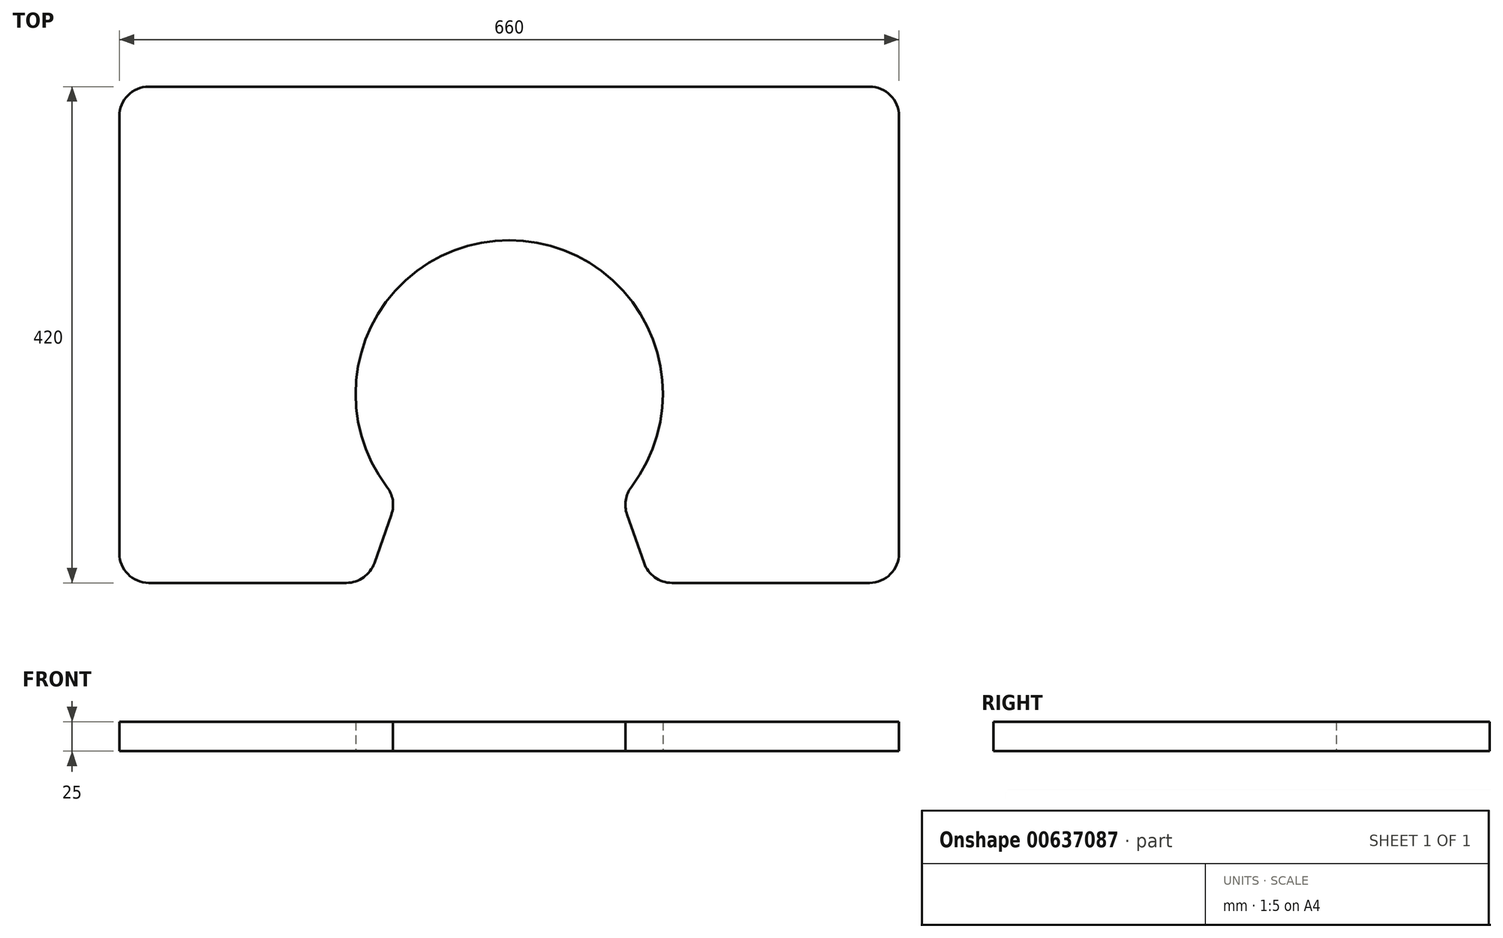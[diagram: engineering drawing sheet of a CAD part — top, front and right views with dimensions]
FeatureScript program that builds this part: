
annotation { "Feature Type Name" : "Feature", "Feature Type Description" : "" }
export const myFeature = defineFeature(function(context is Context, id is Id, definition is map)
    precondition{}
    {
        {
            var Q0;
            Q0=qCreatedBy(makeId("Top.planeOp"),FACE);
            var sketch = newSketch(context, id + "F0", { "sketchPlane" : qUnion([Q0])});
            skLineSegment(sketch, "E0.bottom", {"start": v(330, 210) * mm, "end": v(-330, 210) * mm});
            skLineSegment(sketch, "E0.top", {"start": v(330, -210) * mm, "end": v(-330, -210) * mm});
            skLineSegment(sketch, "E0.left", {"start": v(330, 210) * mm, "end": v(330, -210) * mm});
            skLineSegment(sketch, "E0.right", {"start": v(-330, 210) * mm, "end": v(-330, -210) * mm});
            skPoint(sketch, "E0.middle", {"position": v(0, 0) * mm});
            skCircle(sketch, "E1", {"center": v(0.03, -50) * mm, "radius": 130 * mm});
            skLineSegment(sketch, "E2", {"start": v(-120, -210) * mm, "end": v(-94.96, -138.76) * mm});
            skLineSegment(sketch, "E3", {"start": v(120, -210) * mm, "end": v(95.04, -138.73) * mm});
            skPoint(sketch, "E4", {"position": v(0, -210) * mm});
            skSolve(sketch);
        }
        {
            var Q0;
            Q0=makeQuery(id+"F0.imprint","IMPRINT",FACE,{"disambiguationData":[TD([[makeQuery(id+"F0.imprint","IMPRINT",EDGE,{"derivedFrom":sQuery(id+"F0.wireOp",EDGE,"E0.bottom")}),1.0]])]});
            extrude(context, id + "F1", {"entities" : qUnion([Q0]), "depth" : 25 * mm});
        }
        {
            var Q0;
            Q0=makeQuery(id+"F1.opExtrude","SWEPT_EDGE",EDGE,{"disambiguationData":[OSD([sQuery(id+"F0.wireOp",EDGE,"E1"),sQuery(id+"F0.wireOp",EDGE,"8K2nLb33-7zb7-YIVY-jQB5-7TyeZ0Rkaev6")])]});
            var Q1;
            Q1=makeQuery(id+"F1.opExtrude","SWEPT_EDGE",EDGE,{"disambiguationData":[OSD([sQuery(id+"F0.wireOp",EDGE,"E1"),sQuery(id+"F0.wireOp",EDGE,"b5508e05-085b-4176-a4c3-e73228444c430.MirrorCS")])]});
            var Q2;
            Q2=makeQuery(id+"F1.opExtrude","SWEPT_EDGE",EDGE,{"disambiguationData":[OSD([sQuery(id+"F0.wireOp",EDGE,"E0.top"),sQuery(id+"F0.wireOp",EDGE,"b5508e05-085b-4176-a4c3-e73228444c430.MirrorCS"),sQuery(id+"F0.wireOp",EDGE,"b5508e05-085b-4176-a4c3-e73228444c431.MirrorCS")])]});
            var Q3;
            Q3=makeQuery(id+"F1.opExtrude","SWEPT_EDGE",EDGE,{"disambiguationData":[OSD([sQuery(id+"F0.wireOp",EDGE,"E0.top"),sQuery(id+"F0.wireOp",EDGE,"E0.left")])]});
            var Q4;
            Q4=makeQuery(id+"F1.opExtrude","SWEPT_EDGE",EDGE,{"disambiguationData":[OSD([sQuery(id+"F0.wireOp",EDGE,"E0.top"),sQuery(id+"F0.wireOp",EDGE,"8K2nLb33-7zb7-YIVY-jQB5-7TyeZ0Rkaev6"),sQuery(id+"F0.wireOp",EDGE,"ovbGFed6-ZiOo-55EP-2kew-Z5asyUi1s6AM")])]});
            var Q5;
            Q5=makeQuery(id+"F1.opExtrude","SWEPT_EDGE",EDGE,{"disambiguationData":[OSD([sQuery(id+"F0.wireOp",EDGE,"E0.top"),sQuery(id+"F0.wireOp",EDGE,"E0.right")])]});
            var Q6;
            Q6=makeQuery(id+"F1.opExtrude","SWEPT_EDGE",EDGE,{"disambiguationData":[OSD([sQuery(id+"F0.wireOp",EDGE,"E0.bottom"),sQuery(id+"F0.wireOp",EDGE,"E0.left")])]});
            var Q7;
            Q7=makeQuery(id+"F1.opExtrude","SWEPT_EDGE",EDGE,{"disambiguationData":[OSD([sQuery(id+"F0.wireOp",EDGE,"E0.bottom"),sQuery(id+"F0.wireOp",EDGE,"E0.right")])]});
            fillet(context, id + "F2", {"entities" : qUnion([Q0, Q1, Q2, Q3, Q4, Q5, Q6, Q7]), "radius" : 25 * mm, "tangentPropagation" : true, "allowEdgeOverflow" : false});
        }
    });
